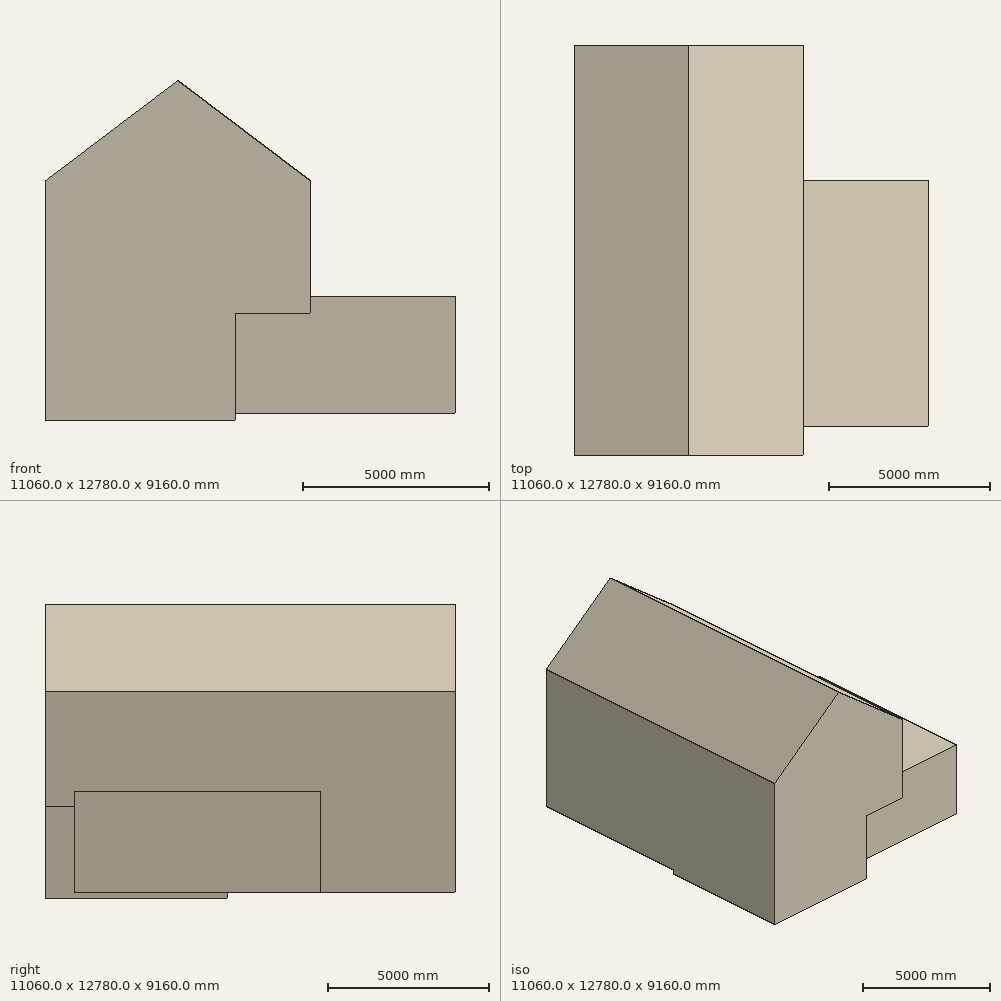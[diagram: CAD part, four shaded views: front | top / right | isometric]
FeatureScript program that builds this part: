
annotation { "Feature Type Name" : "Feature", "Feature Type Description" : "" }
export const myFeature = defineFeature(function(context is Context, id is Id, definition is map)
    precondition{}
    {
        {
            var Q0;
            Q0=qCreatedBy(makeId("Front.planeOp"),FACE);
            var sketch = newSketch(context, id + "F0", { "sketchPlane" : qUnion([Q0])});
            skLineSegment(sketch, "E0", {"start": v(0, 0) * mm, "end": v(0, 5820) * mm});
            skLineSegment(sketch, "E1", {"start": v(0, 5820) * mm, "end": v(3580, 8530) * mm});
            skLineSegment(sketch, "E2", {"start": v(3580, 8530) * mm, "end": v(7160, 5820) * mm});
            skLineSegment(sketch, "E3", {"start": v(7160, 5820) * mm, "end": v(7160, 0) * mm});
            skLineSegment(sketch, "E4", {"start": v(7160, 0) * mm, "end": v(0, 0) * mm});
            skSolve(sketch);
        }
        {
            var Q0;
            Q0 = qSketchRegion(id + "F0", true);
            extrude(context, id + "F1", {"entities" : qUnion([Q0]), "oppositeDirection" : true, "depth" : 12780 * mm});
        }
        {
            var Q0;
            Q0=makeQuery(id+"F1.opExtrude","SWEPT_FACE",FACE,{"disambiguationData":[OSD([sQuery(id+"F0.wireOp",EDGE,"E4")])]});
            var sketch = newSketch(context, id + "F2", { "sketchPlane" : qUnion([Q0])});
            skLineSegment(sketch, "E5.bottom", {"start": v(0, 0) * mm, "end": v(5130, 0) * mm});
            skLineSegment(sketch, "E5.top", {"start": v(0, -5680) * mm, "end": v(5130, -5680) * mm});
            skLineSegment(sketch, "E5.left", {"start": v(0, 0) * mm, "end": v(0, -5680) * mm});
            skLineSegment(sketch, "E5.right", {"start": v(5130, 0) * mm, "end": v(5130, -5680) * mm});
            skSolve(sketch);
        }
        {
            var Q0;
            Q0 = qSketchRegion(id + "F2", true);
            extrude(context, id + "F3", {"entities" : qUnion([Q0]), "operationType" : NewBodyOperationType.ADD, "depth" : 630 * mm});
        }
        {
            var Q0;
            Q0=makeQuery(id+"F1.opExtrude","SWEPT_FACE",FACE,{"disambiguationData":[OSD([sQuery(id+"F0.wireOp",EDGE,"E4")])]});
            var sketch = newSketch(context, id + "F4", { "sketchPlane" : qUnion([Q0])});
            skLineSegment(sketch, "E6.bottom", {"start": v(0, 0) * mm, "end": v(7160, 0) * mm});
            skLineSegment(sketch, "E6.top", {"start": v(0, -12780) * mm, "end": v(7160, -12780) * mm});
            skLineSegment(sketch, "E6.left", {"start": v(0, 0) * mm, "end": v(0, -12780) * mm});
            skLineSegment(sketch, "E6.right", {"start": v(7160, 0) * mm, "end": v(7160, -12780) * mm});
            skSolve(sketch);
        }
        {
            var Q0;
            Q0 = qSketchRegion(id + "F4", true);
            extrude(context, id + "F5", {"entities" : qUnion([Q0]), "operationType" : NewBodyOperationType.ADD, "depth" : 450 * mm});
        }
        {
            var Q0;
            Q0=qCreatedBy(makeId("Top.planeOp"),FACE);
            var sketch = newSketch(context, id + "F6", { "sketchPlane" : qUnion([Q0])});
            skLineSegment(sketch, "E7.bottom", {"start": v(7160, 900) * mm, "end": v(11060, 900) * mm});
            skLineSegment(sketch, "E7.top", {"start": v(7160, 8580) * mm, "end": v(11060, 8580) * mm});
            skLineSegment(sketch, "E7.left", {"start": v(7160, 900) * mm, "end": v(7160, 8580) * mm});
            skLineSegment(sketch, "E7.right", {"start": v(11060, 900) * mm, "end": v(11060, 8580) * mm});
            skSolve(sketch);
        }
        {
            var Q0;
            Q0 = qSketchRegion(id + "F6", true);
            var Q1;
            Q1=makeQuery(id+"F5.opExtrude","CAP_FACE",FACE,{"disambiguationData":[OSD([sQuery(id+"F4.wireOp",EDGE,"E6.bottom"),sQuery(id+"F4.wireOp",EDGE,"E6.top"),sQuery(id+"F4.wireOp",EDGE,"E6.left"),sQuery(id+"F4.wireOp",EDGE,"E6.right")])],"isStart":false});
            extrude(context, id + "F7", {"entities" : qUnion([Q0]), "operationType" : NewBodyOperationType.ADD, "depth" : 2700 * mm, "hasSecondDirection" : true, "secondDirectionBound" : SecondDirectionBoundingType.UP_TO_SURFACE, "secondDirectionOppositeDirection" : true, "secondDirectionBoundEntityFace" : qUnion([Q1]), "secondDirectionDepth" : 25 * mm});
        }
        {
            var Q0;
            Q0=qCreatedBy(makeId("Top.planeOp"),FACE);
            var sketch = newSketch(context, id + "F8", { "sketchPlane" : qUnion([Q0])});
            skLineSegment(sketch, "E8.bottom", {"start": v(7160, 0) * mm, "end": v(5130, 0) * mm});
            skLineSegment(sketch, "E8.top", {"start": v(7160, 900) * mm, "end": v(5130, 900) * mm});
            skLineSegment(sketch, "E8.left", {"start": v(7160, 900) * mm, "end": v(7160, 0) * mm});
            skLineSegment(sketch, "E8.right", {"start": v(5130, 900) * mm, "end": v(5130, 0) * mm});
            skSolve(sketch);
        }
        {
            var Q0;
            Q0 = qSketchRegion(id + "F8", true);
            extrude(context, id + "F9", {"entities" : qUnion([Q0]), "operationType" : NewBodyOperationType.REMOVE, "depth" : 2250 * mm, "hasSecondDirection" : true, "secondDirectionBound" : SecondDirectionBoundingType.UP_TO_NEXT, "secondDirectionOppositeDirection" : true, "secondDirectionDepth" : 25 * mm});
        }
        {
            var Q0;
            Q0=makeQuery(id+"F9.boolean.opBoolean","MERGE",FACE,{"derivedFrom":[makeQuery(id+"F7.opExtrude","SWEPT_FACE",FACE,{"disambiguationData":[OSD([sQuery(id+"F6.wireOp",EDGE,"E7.bottom")])]})],"fromTools":[makeQuery(id+"F9.opExtrude","SWEPT_FACE",FACE,{"disambiguationData":[OSD([sQuery(id+"F8.wireOp",EDGE,"E8.top")])]})]});
            var sketch = newSketch(context, id + "F10", { "sketchPlane" : qUnion([Q0])});
            skLineSegment(sketch, "E9.bottom", {"start": v(9610, 0) * mm, "end": v(10510, 0) * mm});
            skLineSegment(sketch, "E9.top", {"start": v(9610, 2250) * mm, "end": v(10510, 2250) * mm});
            skLineSegment(sketch, "E9.left", {"start": v(9610, 0) * mm, "end": v(9610, 2250) * mm});
            skLineSegment(sketch, "E9.right", {"start": v(10510, 0) * mm, "end": v(10510, 2250) * mm});
            skLineSegment(sketch, "E10", {"start": v(9610, 2250) * mm, "end": v(7130, 2250) * mm});
            skLineSegment(sketch, "E11", {"start": v(7130, 2250) * mm, "end": v(7130, 0) * mm});
            skLineSegment(sketch, "E12", {"start": v(7130, 0) * mm, "end": v(9610, 0) * mm});
            skLineSegment(sketch, "E13", {"start": v(7130, 2250) * mm, "end": v(5130, 2250) * mm});
            skLineSegment(sketch, "E14", {"start": v(5130, 2250) * mm, "end": v(5130, 0) * mm});
            skLineSegment(sketch, "E15", {"start": v(5130, 0) * mm, "end": v(7130, 0) * mm});
            skLineSegment(sketch, "E16", {"start": v(5530, 2250) * mm, "end": v(5530, 0) * mm});
            skLineSegment(sketch, "E17", {"start": v(6430, 2250) * mm, "end": v(6430, 0) * mm});
            skSolve(sketch);
        }
        {
            var Q0;
            Q0=makeQuery(id+"F5.boolean.opBoolean","MERGE",FACE,{"derivedFrom":[makeQuery(id+"F3.boolean.opBoolean","MERGE",FACE,{"derivedFrom":[makeQuery(id+"F1.opExtrude","CAP_FACE",FACE,{"disambiguationData":[OSD([sQuery(id+"F0.wireOp",EDGE,"E0"),sQuery(id+"F0.wireOp",EDGE,"E1"),sQuery(id+"F0.wireOp",EDGE,"E2"),sQuery(id+"F0.wireOp",EDGE,"E3"),sQuery(id+"F0.wireOp",EDGE,"E4")])],"isStart":true}),makeQuery(id+"F3.opExtrude","SWEPT_FACE",FACE,{"disambiguationData":[OSD([sQuery(id+"F2.wireOp",EDGE,"E5.bottom")])]})]}),makeQuery(id+"F5.opExtrude","SWEPT_FACE",FACE,{"disambiguationData":[OSD([sQuery(id+"F4.wireOp",EDGE,"E6.bottom")])]})]});
            var sketch = newSketch(context, id + "F11", { "sketchPlane" : qUnion([Q0])});
            skLineSegment(sketch, "E18.bottom", {"start": v(1150, 2250) * mm, "end": v(2050, 2250) * mm});
            skLineSegment(sketch, "E18.top", {"start": v(1150, 0) * mm, "end": v(2050, 0) * mm});
            skLineSegment(sketch, "E18.left", {"start": v(1150, 2250) * mm, "end": v(1150, 0) * mm});
            skLineSegment(sketch, "E18.right", {"start": v(2050, 2250) * mm, "end": v(2050, 0) * mm});
            skLineSegment(sketch, "E19.bottom", {"start": v(1823.87, 4213.23) * mm, "end": v(3373.87, 4213.23) * mm});
            skLineSegment(sketch, "E19.top", {"start": v(1823.87, 3213.23) * mm, "end": v(3373.87, 3213.23) * mm});
            skLineSegment(sketch, "E19.left", {"start": v(1823.87, 4213.23) * mm, "end": v(1823.87, 3213.23) * mm});
            skLineSegment(sketch, "E19.right", {"start": v(3373.87, 4213.23) * mm, "end": v(3373.87, 3213.23) * mm});
            skLineSegment(sketch, "E20", {"start": v(1150, 0) * mm, "end": v(0, 0) * mm});
            skLineSegment(sketch, "E21", {"start": v(0, 0) * mm, "end": v(0, 2250) * mm});
            skLineSegment(sketch, "E22", {"start": v(0, 2250) * mm, "end": v(1150, 2250) * mm});
            skLineSegment(sketch, "E23", {"start": v(2050, 2250) * mm, "end": v(5130, 2250) * mm});
            skLineSegment(sketch, "E24", {"start": v(5130, 2250) * mm, "end": v(5130, 0) * mm});
            skLineSegment(sketch, "E25", {"start": v(5130, 0) * mm, "end": v(2050, 0) * mm});
            skSolve(sketch);
        }
        {
            var Q0;
            Q0=makeQuery(id+"F9.boolean.opBoolean","MERGE",FACE,{"derivedFrom":[makeQuery(id+"F3.opExtrude","SWEPT_FACE",FACE,{"disambiguationData":[OSD([sQuery(id+"F2.wireOp",EDGE,"E5.right")])]})],"fromTools":[makeQuery(id+"F9.opExtrude","SWEPT_FACE",FACE,{"disambiguationData":[OSD([sQuery(id+"F8.wireOp",EDGE,"E8.right")])]})]});
            var sketch = newSketch(context, id + "F12", { "sketchPlane" : qUnion([Q0])});
            skLineSegment(sketch, "E26.bottom", {"start": v(900, 2250) * mm, "end": v(0, 2250) * mm});
            skLineSegment(sketch, "E26.top", {"start": v(900, 0) * mm, "end": v(0, 0) * mm});
            skLineSegment(sketch, "E26.left", {"start": v(900, 2250) * mm, "end": v(900, 0) * mm});
            skLineSegment(sketch, "E26.right", {"start": v(0, 2250) * mm, "end": v(0, 0) * mm});
            skLineSegment(sketch, "E27.top", {"start": v(900, -630) * mm, "end": v(0, -630) * mm});
            skLineSegment(sketch, "E27.left", {"start": v(900, 0) * mm, "end": v(900, -630) * mm});
            skLineSegment(sketch, "E27.right", {"start": v(0, 0) * mm, "end": v(0, -630) * mm});
            skSolve(sketch);
        }
        {
            var Q0;
            Q0=makeQuery(id+"F5.boolean.opBoolean","MERGE",FACE,{"derivedFrom":[makeQuery(id+"F3.boolean.opBoolean","MERGE",FACE,{"derivedFrom":[makeQuery(id+"F1.opExtrude","SWEPT_FACE",FACE,{"disambiguationData":[OSD([sQuery(id+"F0.wireOp",EDGE,"E0")])]}),makeQuery(id+"F3.opExtrude","SWEPT_FACE",FACE,{"disambiguationData":[OSD([sQuery(id+"F2.wireOp",EDGE,"E5.left")])]})]}),makeQuery(id+"F5.opExtrude","SWEPT_FACE",FACE,{"disambiguationData":[OSD([sQuery(id+"F4.wireOp",EDGE,"E6.left")])]})]});
            var sketch = newSketch(context, id + "F13", { "sketchPlane" : qUnion([Q0])});
            skLineSegment(sketch, "E28.bottom", {"start": v(-3540, 2250) * mm, "end": v(-2190, 2250) * mm});
            skLineSegment(sketch, "E28.left", {"start": v(-3540, 2250) * mm, "end": v(-3540, 220) * mm});
            skLineSegment(sketch, "E28.right", {"start": v(-2190, 2250) * mm, "end": v(-2190, 220) * mm});
            skLineSegment(sketch, "E29.bottom", {"start": v(-10580, 2250) * mm, "end": v(-6610, 2250) * mm});
            skLineSegment(sketch, "E29.top", {"start": v(-10580, 0) * mm, "end": v(-6610, 0) * mm});
            skLineSegment(sketch, "E29.left", {"start": v(-10580, 2250) * mm, "end": v(-10580, 0) * mm});
            skLineSegment(sketch, "E29.right", {"start": v(-6610, 2250) * mm, "end": v(-6610, 0) * mm});
            skLineSegment(sketch, "E30.bottom", {"start": v(-10890.6, 5468.9) * mm, "end": v(-9990.6, 5468.9) * mm});
            skLineSegment(sketch, "E30.top", {"start": v(-10890.6, 3318.9) * mm, "end": v(-9990.6, 3318.9) * mm});
            skLineSegment(sketch, "E30.left", {"start": v(-10890.6, 5468.9) * mm, "end": v(-10890.6, 3318.9) * mm});
            skLineSegment(sketch, "E30.right", {"start": v(-9990.6, 5468.9) * mm, "end": v(-9990.6, 3318.9) * mm});
            skLineSegment(sketch, "E31.bottom", {"start": v(-6435.37, 5468.9) * mm, "end": v(-5535.37, 5468.9) * mm});
            skLineSegment(sketch, "E31.top", {"start": v(-6435.37, 3318.9) * mm, "end": v(-5535.37, 3318.9) * mm});
            skLineSegment(sketch, "E31.left", {"start": v(-6435.37, 5468.9) * mm, "end": v(-6435.37, 3318.9) * mm});
            skLineSegment(sketch, "E31.right", {"start": v(-5535.37, 5468.9) * mm, "end": v(-5535.37, 3318.9) * mm});
            skLineSegment(sketch, "E32.bottom", {"start": v(-2730.04, 5468.9) * mm, "end": v(-1830.04, 5468.9) * mm});
            skLineSegment(sketch, "E32.top", {"start": v(-2730.04, 3318.9) * mm, "end": v(-1830.04, 3318.9) * mm});
            skLineSegment(sketch, "E32.left", {"start": v(-2730.04, 5468.9) * mm, "end": v(-2730.04, 3318.9) * mm});
            skLineSegment(sketch, "E32.right", {"start": v(-1830.04, 5468.9) * mm, "end": v(-1830.04, 3318.9) * mm});
            skLineSegment(sketch, "E33", {"start": v(-6610, 2250) * mm, "end": v(-3540, 2250) * mm});
            skLineSegment(sketch, "E34", {"start": v(-2190, 2250) * mm, "end": v(0, 2250) * mm});
            skLineSegment(sketch, "E35", {"start": v(0, 2250) * mm, "end": v(0, 0) * mm});
            skLineSegment(sketch, "E36", {"start": v(0, 0) * mm, "end": v(-6610, 0) * mm});
            skLineSegment(sketch, "E37", {"start": v(-3540, 220) * mm, "end": v(-2190, 220) * mm});
            skPoint(sketch, "E38.orphan", {"position": v(-2190, 0) * mm});
            skSolve(sketch);
        }
    });
